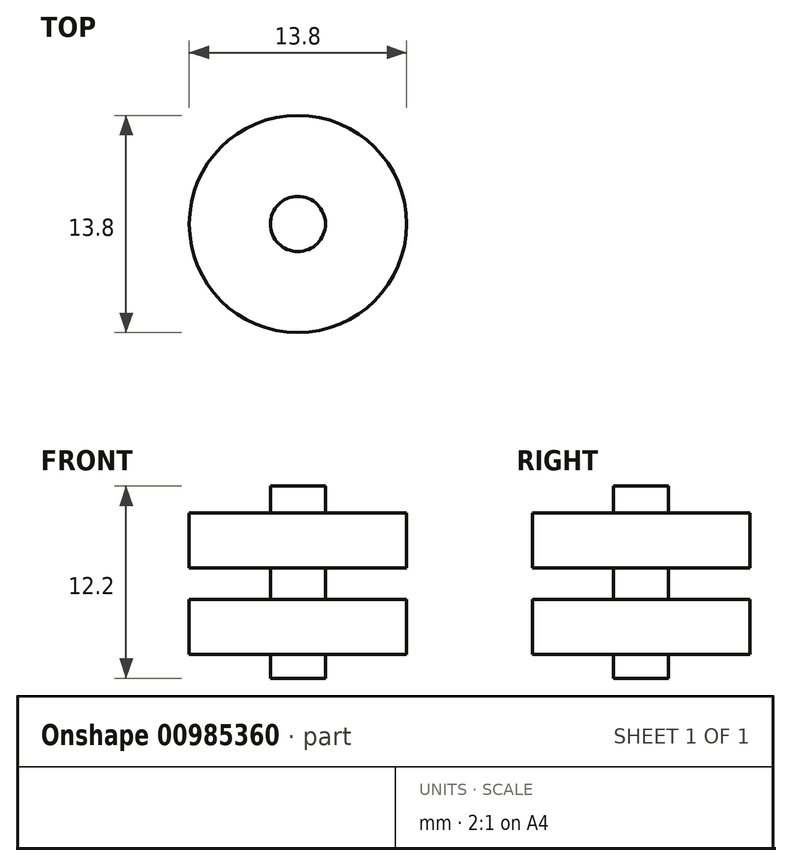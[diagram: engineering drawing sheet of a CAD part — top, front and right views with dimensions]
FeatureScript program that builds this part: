
annotation { "Feature Type Name" : "Feature", "Feature Type Description" : "" }
export const myFeature = defineFeature(function(context is Context, id is Id, definition is map)
    precondition{}
    {
        {
            var Q0;
            Q0=qCreatedBy(makeId("Top.planeOp"),FACE);
            var sketch = newSketch(context, id + "F0", { "sketchPlane" : qUnion([Q0])});
            skCircle(sketch, "E0", {"center": v(0, 0) * mm, "radius": 6.9 * mm});
            skCircle(sketch, "E1", {"center": v(0, 0) * mm, "radius": 1.8 * mm});
            skSolve(sketch);
        }
        {
            var Q0;
            Q0=qCreatedBy(makeId("Top.planeOp"),FACE);
            var sketch = newSketch(context, id + "F1", { "sketchPlane" : qUnion([Q0])});
            skCircle(sketch, "E2", {"center": v(0, 0) * mm, "radius": 6.9 * mm});
            skCircle(sketch, "E3", {"center": v(0, 0) * mm, "radius": 1.75 * mm});
            skSolve(sketch);
        }
        {
            var Q0;
            Q0=makeQuery(id+"F1.imprint","IMPRINT",FACE,{"disambiguationData":[TD([[makeQuery(id+"F1.imprint","IMPRINT",EDGE,{"derivedFrom":sQuery(id+"F1.wireOp",EDGE,"E2")}),1.0]])]});
            var Q1;
            Q1=makeQuery(id+"F1.imprint","IMPRINT",FACE,{"disambiguationData":[TD([[makeQuery(id+"F1.imprint","IMPRINT",EDGE,{"derivedFrom":sQuery(id+"F1.wireOp",EDGE,"E3")}),1.0]])]});
            extrude(context, id + "F2", {"entities" : qUnion([Q0, Q1]), "depth" : 3.5 * mm, "offsetDistance" : 25 * mm});
        }
        {
            var Q0;
            Q0=makeQuery(id+"F1.imprint","IMPRINT",FACE,{"disambiguationData":[TD([[makeQuery(id+"F1.imprint","IMPRINT",EDGE,{"derivedFrom":sQuery(id+"F1.wireOp",EDGE,"E3")}),1.0]])]});
            extrude(context, id + "F3", {"entities" : qUnion([Q0]), "operationType" : NewBodyOperationType.ADD, "depth" : 5.2 * mm, "offsetDistance" : 25 * mm});
        }
        {
            var Q0;
            Q0=makeQuery(id+"F1.imprint","IMPRINT",FACE,{"disambiguationData":[TD([[makeQuery(id+"F1.imprint","IMPRINT",EDGE,{"derivedFrom":sQuery(id+"F1.wireOp",EDGE,"E3")}),1.0]])]});
            var Q1;
            Q1=sQuery(id+"F1.wireOp",EDGE,"E3");
            extrude(context, id + "F4", {"entities" : qUnion([Q0]), "operationType" : NewBodyOperationType.ADD, "surfaceOperationType" : NewSurfaceOperationType.ADD, "surfaceEntities" : qUnion([Q1]), "depth" : -4 * mm, "offsetDistance" : 25 * mm});
        }
        {
            var Q0;
            Q0=makeQuery(id+"F2.opExtrude","SWEPT_BODY",BODY,{"disambiguationData":[OSD([sQuery(id+"F1.wireOp",EDGE,"E2")])]});
            transform(context, id + "F5", {"entities" : qUnion([Q0]), "transformType" : TransformType.TRANSLATION_3D, "dx" : 0 * mm, "dy" : 0 * mm, "dz" : 2 * mm, "makeCopy" : false});
        }
        {
            var Q0;
            Q0=makeQuery(id+"F1.imprint","IMPRINT",FACE,{"disambiguationData":[TD([[makeQuery(id+"F1.imprint","IMPRINT",EDGE,{"derivedFrom":sQuery(id+"F1.wireOp",EDGE,"E2")}),1.0]])]});
            extrude(context, id + "F6", {"entities" : qUnion([Q0]), "depth" : -3.5 * mm, "offsetDistance" : 25 * mm});
        }
        {
            var Q0;
            Q0=makeQuery(id+"F4.opExtrude","CAP_FACE",FACE,{"disambiguationData":[OSD([sQuery(id+"F1.wireOp",EDGE,"E3")])],"isStart":false});
            var Q1;
            Q1=sQuery(id+"F0.wireOp",EDGE,"E1");
            extrude(context, id + "F7", {"entities" : qUnion([Q0]), "operationType" : NewBodyOperationType.ADD, "surfaceOperationType" : NewSurfaceOperationType.ADD, "surfaceEntities" : qUnion([Q1]), "depth" : -0.5 * mm, "offsetDistance" : 25 * mm, "hasSecondDirection" : true, "secondDirectionOppositeDirection" : true, "secondDirectionDepth" : -3 * mm});
        }
    });
